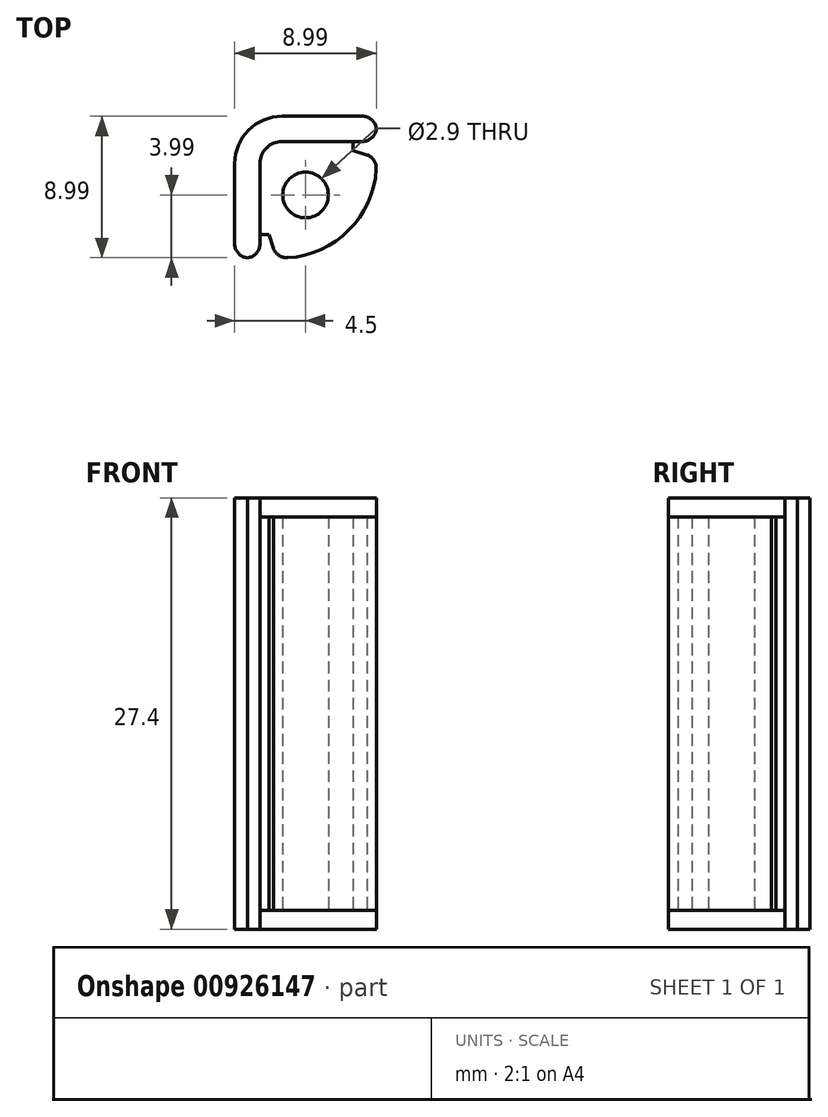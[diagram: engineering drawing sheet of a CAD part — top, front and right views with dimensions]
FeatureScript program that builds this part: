
annotation { "Feature Type Name" : "Feature", "Feature Type Description" : "" }
export const myFeature = defineFeature(function(context is Context, id is Id, definition is map)
    precondition{}
    {
        {
            var Q0;
            Q0=qCreatedBy(makeId("Top.planeOp"),FACE);
            var sketch = newSketch(context, id + "F0", { "sketchPlane" : qUnion([Q0])});
            skLineSegment(sketch, "E0.bottom", {"start": v(-1.5, -4.5) * mm, "end": v(-2.1, -4.5) * mm});
            skLineSegment(sketch, "E0.top", {"start": v(4.5, 4.5) * mm, "end": v(-1.5, 4.5) * mm});
            skLineSegment(sketch, "E0.left", {"start": v(4.5, 1.5) * mm, "end": v(4.5, 2.1) * mm});
            skLineSegment(sketch, "E0.right", {"start": v(-4.5, -4.5) * mm, "end": v(-4.5, 1.5) * mm});
            skPoint(sketch, "E0.middle", {"position": v(0, 0) * mm});
            skPoint(sketch, "E1.visualSharp", {"position": v(-4.5, 4.5) * mm});
            skArc(sketch, "E1.filletArc", {"start": v(-1.5, 4.5) * mm, "mid": v(-3.62, 3.62) * mm, "end": v(-4.5, 1.5) * mm});
            skLineSegment(sketch, "E2.0", {"start": v(4.5, 2.9) * mm, "end": v(-1.5, 2.9) * mm});
            skArc(sketch, "E2.1", {"start": v(-1.5, 2.9) * mm, "mid": v(-2.49, 2.49) * mm, "end": v(-2.9, 1.5) * mm});
            skLineSegment(sketch, "E2.2", {"start": v(-2.9, -4.5) * mm, "end": v(-2.9, 1.5) * mm});
            skCircle(sketch, "E3", {"center": v(0, -0.5) * mm, "radius": 1.45 * mm});
            skLineSegment(sketch, "E4.top", {"start": v(-2.9, -3) * mm, "end": v(-2.1, -3) * mm});
            skLineSegment(sketch, "E4.left", {"start": v(-2.9, -4.5) * mm, "end": v(-2.9, -3) * mm});
            skLineSegment(sketch, "E4.right", {"start": v(-2.1, -4.5) * mm, "end": v(-2.1, -3) * mm});
            skLineSegment(sketch, "E5.bottom", {"start": v(4.5, 2.9) * mm, "end": v(3, 2.9) * mm});
            skLineSegment(sketch, "E5.top", {"start": v(4.5, 2.1) * mm, "end": v(3, 2.1) * mm});
            skLineSegment(sketch, "E5.right", {"start": v(3, 2.9) * mm, "end": v(3, 2.1) * mm});
            skLineSegment(sketch, "E6.trimOffspring", {"start": v(-2.9, -4.5) * mm, "end": v(-4.5, -4.5) * mm});
            skLineSegment(sketch, "E7.trimOffspring", {"start": v(4.5, 2.9) * mm, "end": v(4.5, 4.5) * mm});
            skPoint(sketch, "E8.visualSharp", {"position": v(4.5, -4.5) * mm});
            skArc(sketch, "E8.filletArc", {"start": v(-1.5, -4.5) * mm, "mid": v(2.74, -2.74) * mm, "end": v(4.5, 1.5) * mm});
            skSolve(sketch);
        }
        {
            var Q0;
            Q0=makeQuery(id+"F0.imprint","IMPRINT",FACE,{"disambiguationData":[TD([[makeQuery(id+"F0.imprint","IMPRINT",EDGE,{"derivedFrom":sQuery(id+"F0.wireOp",EDGE,"E0.bottom")}),-1.0]])]});
            var Q1;
            Q1=makeQuery(id+"F0.imprint","IMPRINT",FACE,{"disambiguationData":[TD([[makeQuery(id+"F0.imprint","IMPRINT",EDGE,{"derivedFrom":sQuery(id+"F0.wireOp",EDGE,"E0.top")}),1.0]])]});
            extrude(context, id + "F1", {"entities" : qUnion([Q0, Q1]), "depth" : 25 * mm, "offsetDistance" : 25 * mm});
        }
        {
            var Q0;
            Q0=makeQuery(id+"F0.imprint","IMPRINT",FACE,{"disambiguationData":[TD([[makeQuery(id+"F0.imprint","IMPRINT",EDGE,{"derivedFrom":sQuery(id+"F0.wireOp",EDGE,"E0.top")}),1.0]])]});
            extrude(context, id + "F2", {"entities" : qUnion([Q0]), "operationType" : NewBodyOperationType.ADD, "oppositeDirection" : true, "depth" : 1.2 * mm, "offsetDistance" : 25 * mm, "hasSecondDirection" : true, "secondDirectionOppositeDirection" : false, "secondDirectionDepth" : 26.2 * mm});
        }
        {
            var Q0;
            {var subQ0=sQuery(id+"F0.wireOp",EDGE,"E6.trimOffspring");var subQ1=sQuery(id+"F0.wireOp",EDGE,"E4.left");Q0=makeQuery(id+"F2.boolean.opBoolean","MERGE",EDGE,{"derivedFrom":[makeQuery(id+"F1.opExtrude","SWEPT_EDGE",EDGE,{"disambiguationData":[OSD([subQ1,subQ0])]}),makeQuery(id+"F2.opExtrude","SWEPT_EDGE",EDGE,{"disambiguationData":[OSD([subQ1,subQ0])]})]});}
            var Q1;
            {var subQ0=sQuery(id+"F0.wireOp",EDGE,"E7.trimOffspring");var subQ1=sQuery(id+"F0.wireOp",EDGE,"E5.bottom");Q1=makeQuery(id+"F2.boolean.opBoolean","MERGE",EDGE,{"derivedFrom":[makeQuery(id+"F1.opExtrude","SWEPT_EDGE",EDGE,{"disambiguationData":[OSD([subQ1,subQ0])]}),makeQuery(id+"F2.opExtrude","SWEPT_EDGE",EDGE,{"disambiguationData":[OSD([subQ1,subQ0])]})]});}
            var Q2;
            Q2=makeQuery(id+"F1.opExtrude","SWEPT_EDGE",EDGE,{"disambiguationData":[OSD([sQuery(id+"F0.wireOp",EDGE,"E0.left"),sQuery(id+"F0.wireOp",EDGE,"E5.top")])]});
            var Q3;
            Q3=makeQuery(id+"F1.opExtrude","SWEPT_EDGE",EDGE,{"disambiguationData":[OSD([sQuery(id+"F0.wireOp",EDGE,"E0.bottom"),sQuery(id+"F0.wireOp",EDGE,"E4.right")])]});
            var Q4;
            {var subQ0=sQuery(id+"F0.wireOp",EDGE,"E7.trimOffspring");var subQ1=sQuery(id+"F0.wireOp",EDGE,"E0.top");Q4=makeQuery(id+"F2.boolean.opBoolean","MERGE",EDGE,{"derivedFrom":[makeQuery(id+"F1.opExtrude","SWEPT_EDGE",EDGE,{"disambiguationData":[OSD([subQ1,subQ0])]}),makeQuery(id+"F2.opExtrude","SWEPT_EDGE",EDGE,{"disambiguationData":[OSD([subQ1,subQ0])]})]});}
            var Q5;
            {var subQ0=sQuery(id+"F0.wireOp",EDGE,"E6.trimOffspring");var subQ1=sQuery(id+"F0.wireOp",EDGE,"E0.right");Q5=makeQuery(id+"F2.boolean.opBoolean","MERGE",EDGE,{"derivedFrom":[makeQuery(id+"F1.opExtrude","SWEPT_EDGE",EDGE,{"disambiguationData":[OSD([subQ1,subQ0])]}),makeQuery(id+"F2.opExtrude","SWEPT_EDGE",EDGE,{"disambiguationData":[OSD([subQ1,subQ0])]})]});}
            fillet(context, id + "F3", {"entities" : qUnion([Q0, Q1, Q2, Q3, Q4, Q5]), "radius" : 0.9 * mm, "tangentPropagation" : true, "allowEdgeOverflow" : false});
        }
        {
            var Q0;
            Q0=makeQuery(id+"F1.opExtrude","SWEPT_EDGE",EDGE,{"disambiguationData":[OSD([sQuery(id+"F0.wireOp",EDGE,"E4.top"),sQuery(id+"F0.wireOp",EDGE,"E4.right")])]});
            chamfer(context, id + "F4", {"entities" : qUnion([Q0]), "chamferType" : ChamferType.TWO_OFFSETS, "width1" : 1 * mm, "oppositeDirection" : false, "width2" : 0.3 * mm, "tangentPropagation" : true});
        }
        {
            var Q0;
            Q0=makeQuery(id+"F1.opExtrude","SWEPT_EDGE",EDGE,{"disambiguationData":[OSD([sQuery(id+"F0.wireOp",EDGE,"E5.top"),sQuery(id+"F0.wireOp",EDGE,"E5.right")])]});
            chamfer(context, id + "F5", {"entities" : qUnion([Q0]), "chamferType" : ChamferType.TWO_OFFSETS, "width1" : 0.3 * mm, "oppositeDirection" : false, "width2" : 1 * mm, "tangentPropagation" : true});
        }
    });
